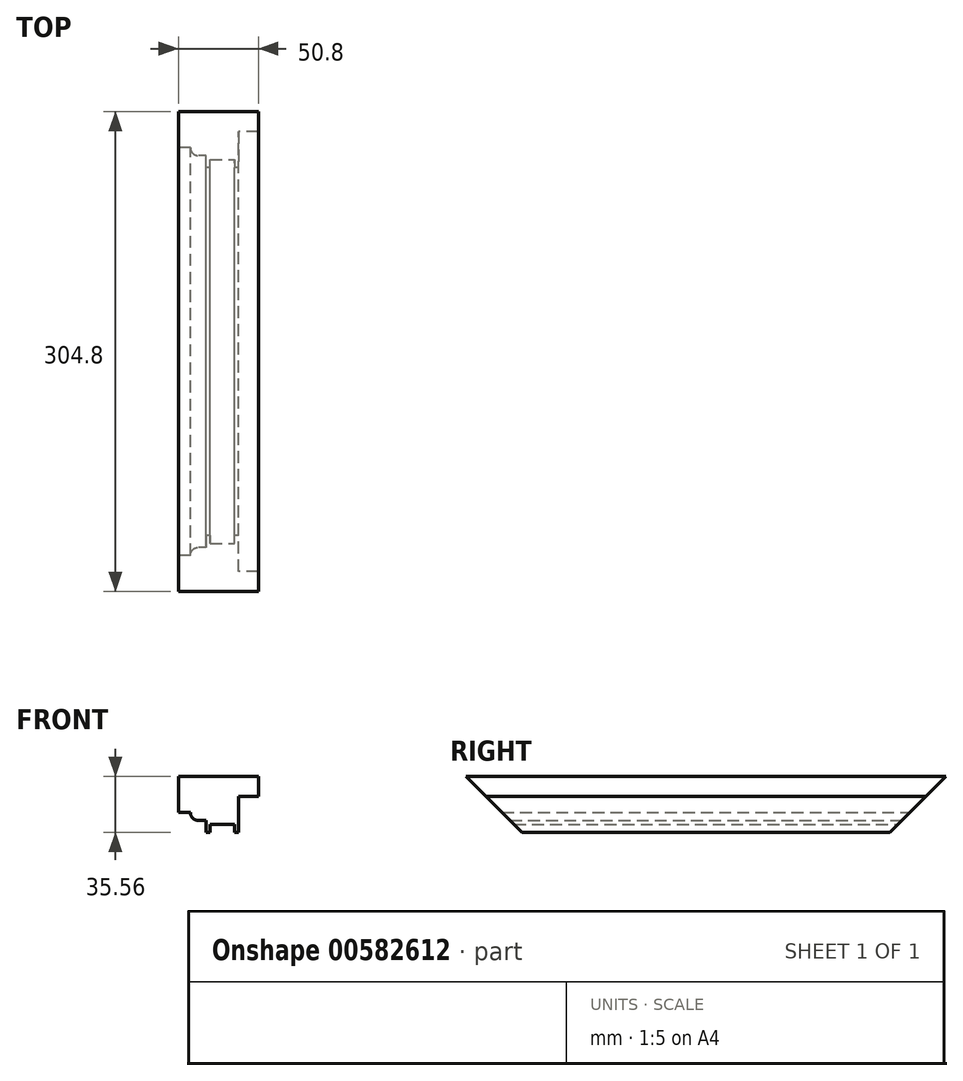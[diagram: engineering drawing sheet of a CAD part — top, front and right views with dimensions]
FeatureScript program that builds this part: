
annotation { "Feature Type Name" : "Feature", "Feature Type Description" : "" }
export const myFeature = defineFeature(function(context is Context, id is Id, definition is map)
    precondition{}
    {
        {
            var Q0;
            Q0=qCreatedBy(makeId("Front.planeOp"),FACE);
            var sketch = newSketch(context, id + "F0", { "sketchPlane" : qUnion([Q0])});
            skLineSegment(sketch, "E0", {"start": v(0, 0) * mm, "end": v(50.8, 0) * mm});
            skLineSegment(sketch, "E1", {"start": v(50.8, 0) * mm, "end": v(50.8, -12.7) * mm});
            skLineSegment(sketch, "E2", {"start": v(50.8, -12.7) * mm, "end": v(38.1, -12.7) * mm});
            skLineSegment(sketch, "E3", {"start": v(38.1, -12.7) * mm, "end": v(38.1, -35.56) * mm});
            skLineSegment(sketch, "E4", {"start": v(17.78, -35.56) * mm, "end": v(17.78, -27.94) * mm});
            skLineSegment(sketch, "E5", {"start": v(17.78, -27.94) * mm, "end": v(7.62, -27.94) * mm});
            skLineSegment(sketch, "E6", {"start": v(7.62, -27.94) * mm, "end": v(7.62, -22.86) * mm});
            skLineSegment(sketch, "E7", {"start": v(7.62, -22.86) * mm, "end": v(0, -22.86) * mm});
            skLineSegment(sketch, "E8", {"start": v(0, -22.86) * mm, "end": v(0, 0) * mm});
            skLineSegment(sketch, "E9", {"start": v(17.78, -35.56) * mm, "end": v(20.32, -35.56) * mm});
            skLineSegment(sketch, "E10", {"start": v(20.32, -35.56) * mm, "end": v(20.32, -30.48) * mm});
            skLineSegment(sketch, "E11", {"start": v(20.32, -30.48) * mm, "end": v(35.56, -30.48) * mm});
            skLineSegment(sketch, "E12", {"start": v(35.56, -30.48) * mm, "end": v(35.56, -35.56) * mm});
            skLineSegment(sketch, "E13", {"start": v(35.56, -35.56) * mm, "end": v(38.1, -35.56) * mm});
            skSolve(sketch);
        }
        {
            var Q0;
            Q0 = qSketchRegion(id + "F0", true);
            extrude(context, id + "F1", {"entities" : qUnion([Q0]), "depth" : 304.8 * mm, "offsetDistance" : 25.4 * mm});
        }
        {
            var Q0;
            Q0=makeQuery(id+"F1.opExtrude","SWEPT_FACE",FACE,{"disambiguationData":[OSD([sQuery(id+"F0.wireOp",EDGE,"E8")])]});
            var sketch = newSketch(context, id + "F2", { "sketchPlane" : qUnion([Q0])});
            skLineSegment(sketch, "E14", {"start": v(0, 0) * mm, "end": v(0, -35.56) * mm});
            skLineSegment(sketch, "E15", {"start": v(0, -35.56) * mm, "end": v(35.56, -35.56) * mm});
            skLineSegment(sketch, "E16", {"start": v(35.56, -35.56) * mm, "end": v(0, 0) * mm});
            skLineSegment(sketch, "E17", {"start": v(304.8, 0) * mm, "end": v(304.8, -35.56) * mm});
            skLineSegment(sketch, "E18", {"start": v(304.8, -35.56) * mm, "end": v(269.24, -35.56) * mm});
            skLineSegment(sketch, "E19", {"start": v(269.24, -35.56) * mm, "end": v(304.8, 0) * mm});
            skSolve(sketch);
        }
        {
            var Q0;
            Q0 = qSketchRegion(id + "F2", true);
            extrude(context, id + "F3", {"entities" : qUnion([Q0]), "operationType" : NewBodyOperationType.REMOVE, "oppositeDirection" : true, "depth" : 50.8 * mm, "offsetDistance" : 25.4 * mm});
        }
        {
            var Q0;
            Q0=makeQuery(id+"F1.opExtrude","SWEPT_EDGE",EDGE,{"disambiguationData":[OSD([sQuery(id+"F0.wireOp",EDGE,"E5"),sQuery(id+"F0.wireOp",EDGE,"E6")])]});
            fillet(context, id + "F4", {"entities" : qUnion([Q0]), "radius" : 5.08 * mm, "tangentPropagation" : true, "allowEdgeOverflow" : false});
        }
    });
